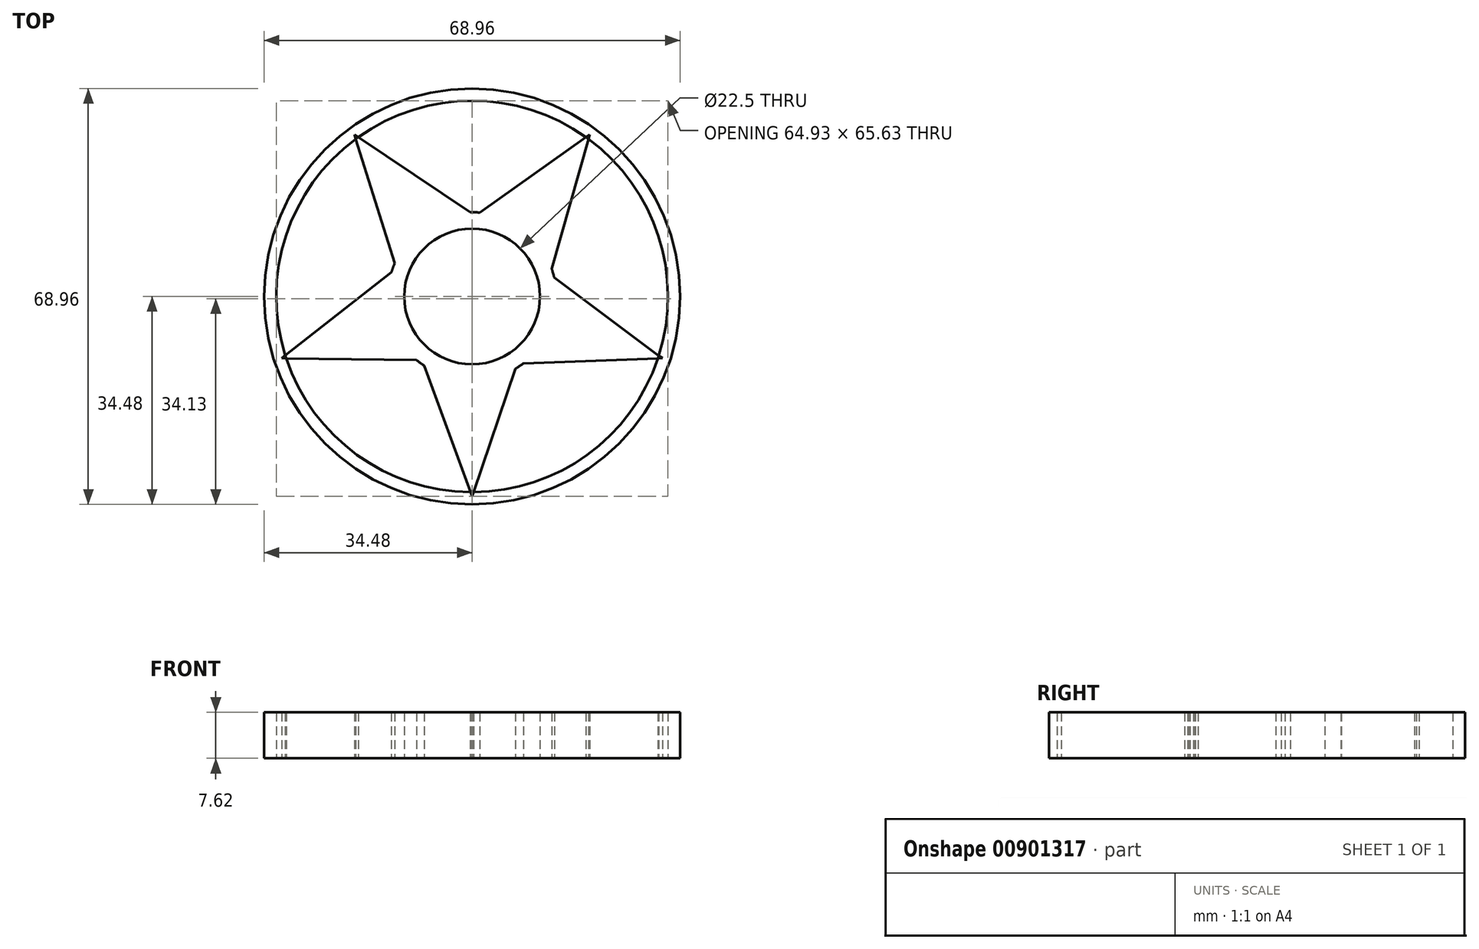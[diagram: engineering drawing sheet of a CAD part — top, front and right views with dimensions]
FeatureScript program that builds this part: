
annotation { "Feature Type Name" : "Feature", "Feature Type Description" : "" }
export const myFeature = defineFeature(function(context is Context, id is Id, definition is map)
    precondition{}
    {
        {
            var Q0;
            Q0=qCreatedBy(makeId("Top.planeOp"),FACE);
            var sketch = newSketch(context, id + "F0", { "sketchPlane" : qUnion([Q0])});
            skCircle(sketch, "E0", {"center": v(0, 0) * mm, "radius": 11.25 * mm});
            skCircle(sketch, "E1", {"center": v(0, 0) * mm, "radius": 13.97 * mm});
            skLineSegment(sketch, "E2", {"start": v(7.16, -12) * mm, "end": v(0, -33.17) * mm});
            skLineSegment(sketch, "E3", {"start": v(0, -33.17) * mm, "end": v(-7.94, -11.5) * mm});
            skLineSegment(sketch, "E4.1.0", {"start": v(31.54, -10.25) * mm, "end": v(8.48, -11.1) * mm});
            skLineSegment(sketch, "E4.1.1", {"start": v(13.62, 3.1) * mm, "end": v(31.54, -10.25) * mm});
            skLineSegment(sketch, "E4.2.0", {"start": v(19.5, 26.83) * mm, "end": v(13.18, 4.63) * mm});
            skLineSegment(sketch, "E4.2.1", {"start": v(1.26, 13.91) * mm, "end": v(19.5, 26.83) * mm});
            skLineSegment(sketch, "E4.3.0", {"start": v(-19.5, 26.83) * mm, "end": v(-0.33, 13.97) * mm});
            skLineSegment(sketch, "E4.3.1", {"start": v(-12.84, 5.5) * mm, "end": v(-19.5, 26.83) * mm});
            skLineSegment(sketch, "E4.4.0", {"start": v(-31.54, -10.25) * mm, "end": v(-13.39, 4) * mm});
            skLineSegment(sketch, "E4.4.1", {"start": v(-9.2, -10.51) * mm, "end": v(-31.54, -10.25) * mm});
            skCircle(sketch, "E5", {"center": v(0, 0) * mm, "radius": 32.47 * mm});
            skCircle(sketch, "E6", {"center": v(0, 0) * mm, "radius": 34.48 * mm});
            skSolve(sketch);
        }
        {
            var Q0;
            {var subQ0=sQuery(id+"F0.wireOp",EDGE,"E4.3.0");var subQ1=sQuery(id+"F0.wireOp",EDGE,"E1");var subQ2=makeQuery(id+"F0.imprint","INTERSECT",VERTEX,{"derivedFrom":[subQ1,subQ0]});Q0=makeQuery(id+"F0.imprint","IMPRINT",FACE,{"disambiguationData":[TD([[makeQuery(id+"F0.imprint","IMPRINT",EDGE,{"disambiguationData":[TD([[subQ2,-1.0]])],"derivedFrom":subQ1}),-1.0]])]});}
            var Q1;
            {var subQ0=sQuery(id+"F0.wireOp",EDGE,"E4.2.0");var subQ1=sQuery(id+"F0.wireOp",EDGE,"E1");var subQ2=makeQuery(id+"F0.imprint","INTERSECT",VERTEX,{"derivedFrom":[subQ1,subQ0]});Q1=makeQuery(id+"F0.imprint","IMPRINT",FACE,{"disambiguationData":[TD([[makeQuery(id+"F0.imprint","IMPRINT",EDGE,{"disambiguationData":[TD([[subQ2,-1.0]])],"derivedFrom":subQ1}),-1.0]])]});}
            var Q2;
            {var subQ0=sQuery(id+"F0.wireOp",EDGE,"E4.1.0");var subQ1=sQuery(id+"F0.wireOp",EDGE,"E1");var subQ2=makeQuery(id+"F0.imprint","INTERSECT",VERTEX,{"derivedFrom":[subQ1,subQ0]});Q2=makeQuery(id+"F0.imprint","IMPRINT",FACE,{"disambiguationData":[TD([[makeQuery(id+"F0.imprint","IMPRINT",EDGE,{"disambiguationData":[TD([[subQ2,-1.0]])],"derivedFrom":subQ1}),-1.0]])]});}
            var Q3;
            {var subQ0=sQuery(id+"F0.wireOp",EDGE,"E2");var subQ1=sQuery(id+"F0.wireOp",EDGE,"E1");var subQ2=makeQuery(id+"F0.imprint","INTERSECT",VERTEX,{"derivedFrom":[subQ1,subQ0]});Q3=makeQuery(id+"F0.imprint","IMPRINT",FACE,{"disambiguationData":[TD([[makeQuery(id+"F0.imprint","IMPRINT",EDGE,{"disambiguationData":[TD([[subQ2,1.0]])],"derivedFrom":subQ1}),-1.0]])]});}
            var Q4;
            {var subQ0=sQuery(id+"F0.wireOp",EDGE,"E4.4.0");var subQ1=sQuery(id+"F0.wireOp",EDGE,"E1");var subQ2=makeQuery(id+"F0.imprint","INTERSECT",VERTEX,{"derivedFrom":[subQ1,subQ0]});Q4=makeQuery(id+"F0.imprint","IMPRINT",FACE,{"disambiguationData":[TD([[makeQuery(id+"F0.imprint","IMPRINT",EDGE,{"disambiguationData":[TD([[subQ2,-1.0]])],"derivedFrom":subQ1}),-1.0]])]});}
            var Q5;
            Q5=makeQuery(id+"F0.imprint","IMPRINT",FACE,{"disambiguationData":[TD([[makeQuery(id+"F0.imprint","IMPRINT",EDGE,{"derivedFrom":sQuery(id+"F0.wireOp",EDGE,"E0")}),-1.0]])]});
            var Q6;
            Q6=makeQuery(id+"F0.imprint","IMPRINT",FACE,{"disambiguationData":[TD([[makeQuery(id+"F0.imprint","IMPRINT",EDGE,{"derivedFrom":sQuery(id+"F0.wireOp",EDGE,"E6")}),1.0]])]});
            extrude(context, id + "F1", {"entities" : qUnion([Q0, Q1, Q2, Q3, Q4, Q5, Q6]), "depth" : 7.62 * mm, "offsetDistance" : 25.4 * mm});
        }
    });
